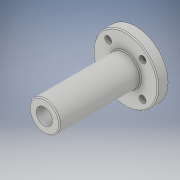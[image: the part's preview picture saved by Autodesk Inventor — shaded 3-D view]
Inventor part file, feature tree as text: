
AUTODESK INVENTOR PART (.ipt)
format: ipt  version: 2018 (Build 220112000, 112)  size: 172,032 bytes
history: native  units: in
note: dims shown in document units (in); Inventor stores cm internally (conversion verified against a paired STEP export)
features: sketch x4, extrude x3, revolve x1, fillet x1
ambient origin geometry x8: Origin, YZ Plane, XZ Plane, XY Plane, X Axis, Y Axis, Z Axis, Center Point
bodies: Solid1 (feature_tree)
feature tree (9):
  revolve  "Revolution1"  [1 undecoded]
  extrude  "Extrusion1"  Depth=0.6299in
  extrude  "Extrusion2"  Depth=0.315in
  extrude  "Extrusion3"  Depth=0.0197in
  fillet  "Fillet1"  Radius=0.4724in
  sketch  "Sketch1"  dims[d0=0.2953in d1=0.1969in]
  sketch  "Sketch2"  dims[d2=90.0deg d3=0.6299in]
  sketch  "Sketch3"  dims[d4=1.7717in d5=0.315in]
  sketch  "Sketch4"  dims[d6=0.3937in d7=0.0in d8=0.1339in d9=0.4724in d10=45.0deg d11=1.5748in d13=360.0deg d15=0.3937in d16=0.0in d17=0.2559in d18=1.5748in d20=360.0deg d22=0.1299in d23=0.0in d24=0.0197in]
note: 1 required parameter value undecoded (feature->parameter linkage not recoverable at this tier; creation-order binding heuristic only, values carry confidence <= 0.55)
